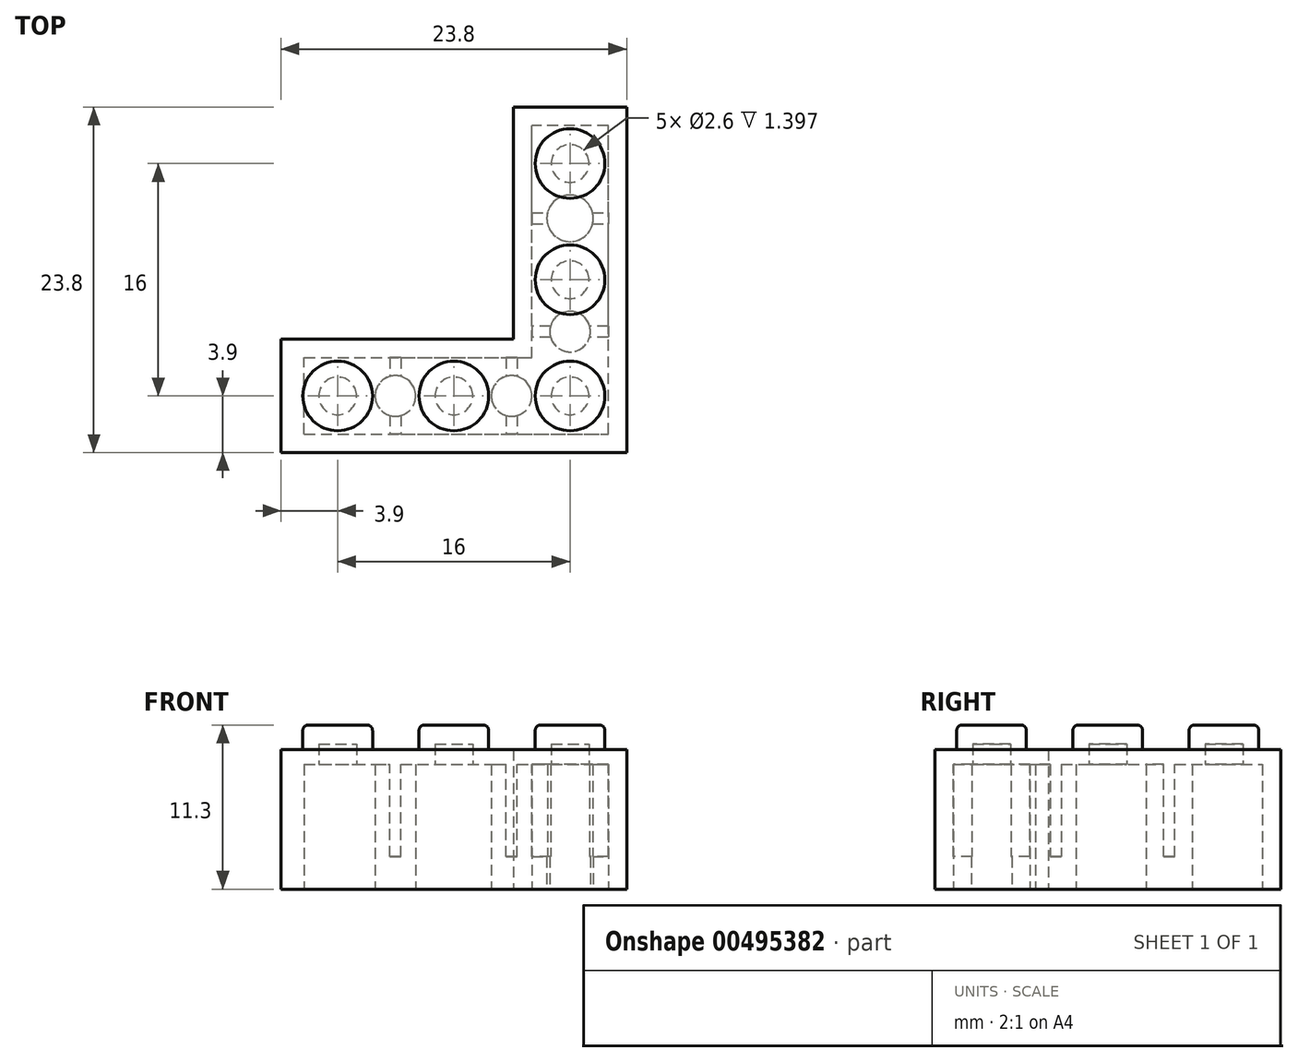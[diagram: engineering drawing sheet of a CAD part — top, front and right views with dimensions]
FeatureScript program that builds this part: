
annotation { "Feature Type Name" : "Feature", "Feature Type Description" : "" }
export const myFeature = defineFeature(function(context is Context, id is Id, definition is map)
    precondition{}
    {
        {
            var Q0;
            Q0=qCreatedBy(makeId("Top.planeOp"),FACE);
            var sketch = newSketch(context, id + "F0", { "sketchPlane" : qUnion([Q0])});
            skLineSegment(sketch, "E0.bottom", {"start": v(-16, 0) * mm, "end": v(0, 0) * mm});
            skLineSegment(sketch, "E0.top", {"start": v(-16, -7.8) * mm, "end": v(7.8, -7.8) * mm});
            skLineSegment(sketch, "E0.left", {"start": v(-16, 0) * mm, "end": v(-16, -7.8) * mm});
            skLineSegment(sketch, "E0.right", {"start": v(7.8, 0) * mm, "end": v(7.8, -7.8) * mm});
            skLineSegment(sketch, "E1.top", {"start": v(7.8, 16) * mm, "end": v(0, 16) * mm});
            skLineSegment(sketch, "E1.left", {"start": v(7.8, 0) * mm, "end": v(7.8, 16) * mm});
            skLineSegment(sketch, "E1.right", {"start": v(0, 0) * mm, "end": v(0, 16) * mm});
            skSolve(sketch);
        }
        {
            var Q0;
            Q0=makeQuery(id+"F0.imprint","IMPRINT",FACE,{"disambiguationData":[TD([[makeQuery(id+"F0.imprint","IMPRINT",EDGE,{"derivedFrom":sQuery(id+"F0.wireOp",EDGE,"E0.bottom")}),-1.0]])]});
            extrude(context, id + "F1", {"entities" : qUnion([Q0]), "depth" : 9.6 * mm});
        }
        {
            var Q0;
            Q0=makeQuery(id+"F1.opExtrude","CAP_FACE",FACE,{"disambiguationData":[OSD([sQuery(id+"F0.wireOp",EDGE,"E0.bottom"),sQuery(id+"F0.wireOp",EDGE,"E0.top"),sQuery(id+"F0.wireOp",EDGE,"E0.left"),sQuery(id+"F0.wireOp",EDGE,"E0.right"),sQuery(id+"F0.wireOp",EDGE,"E1.top"),sQuery(id+"F0.wireOp",EDGE,"E1.left"),sQuery(id+"F0.wireOp",EDGE,"E1.right")])],"isStart":false});
            var sketch = newSketch(context, id + "F2", { "sketchPlane" : qUnion([Q0])});
            skCircle(sketch, "E2", {"center": v(-12.1, -3.9) * mm, "radius": 2.4 * mm});
            skCircle(sketch, "E3", {"center": v(-4.1, -3.9) * mm, "radius": 2.4 * mm});
            skCircle(sketch, "E4", {"center": v(3.9, -3.9) * mm, "radius": 2.4 * mm});
            skCircle(sketch, "E5", {"center": v(3.9, 4.1) * mm, "radius": 2.4 * mm});
            skCircle(sketch, "E6", {"center": v(3.9, 12.1) * mm, "radius": 2.4 * mm});
            skLineSegment(sketch, "E7", {"start": v(-16, -3.9) * mm, "end": v(7.8, -3.9) * mm, "construction": true});
            skLineSegment(sketch, "E8", {"start": v(3.9, 16) * mm, "end": v(3.9, -7.8) * mm, "construction": true});
            skSolve(sketch);
        }
        {
            var Q0;
            Q0=qSketchRegion(id+"F2",true);
            extrude(context, id + "F3", {"entities" : qUnion([Q0]), "operationType" : NewBodyOperationType.ADD, "depth" : 1.7 * mm});
        }
        {
            var Q0;
            Q0=makeQuery(id+"F3.opExtrude","CAP_EDGE",EDGE,{"disambiguationData":[OSD([sQuery(id+"F2.wireOp",EDGE,"E6")])],"isStart":false});
            var Q1;
            Q1=makeQuery(id+"F3.opExtrude","CAP_EDGE",EDGE,{"disambiguationData":[OSD([sQuery(id+"F2.wireOp",EDGE,"E5")])],"isStart":false});
            var Q2;
            Q2=makeQuery(id+"F3.opExtrude","CAP_EDGE",EDGE,{"disambiguationData":[OSD([sQuery(id+"F2.wireOp",EDGE,"E4")])],"isStart":false});
            var Q3;
            Q3=makeQuery(id+"F3.opExtrude","CAP_EDGE",EDGE,{"disambiguationData":[OSD([sQuery(id+"F2.wireOp",EDGE,"E3")])],"isStart":false});
            var Q4;
            Q4=makeQuery(id+"F3.opExtrude","CAP_EDGE",EDGE,{"disambiguationData":[OSD([sQuery(id+"F2.wireOp",EDGE,"E2")])],"isStart":false});
            fillet(context, id + "F4", {"entities" : qUnion([Q0, Q1, Q2, Q3, Q4]), "radius" : 0.38 * mm, "tangentPropagation" : true, "allowEdgeOverflow" : false});
        }
        {
            var Q0;
            Q0=makeQuery(id+"F1.opExtrude","CAP_FACE",FACE,{"disambiguationData":[OSD([sQuery(id+"F0.wireOp",EDGE,"E0.bottom"),sQuery(id+"F0.wireOp",EDGE,"E0.top"),sQuery(id+"F0.wireOp",EDGE,"E0.left"),sQuery(id+"F0.wireOp",EDGE,"E0.right"),sQuery(id+"F0.wireOp",EDGE,"E1.top"),sQuery(id+"F0.wireOp",EDGE,"E1.left"),sQuery(id+"F0.wireOp",EDGE,"E1.right")])],"isStart":true});
            var sketch = newSketch(context, id + "F5", { "sketchPlane" : qUnion([Q0])});
            skLineSegment(sketch, "E9.bottom", {"start": v(-14.4, 6.53) * mm, "end": v(6.53, 6.53) * mm});
            skLineSegment(sketch, "E9.top", {"start": v(-14.4, 1.27) * mm, "end": v(1.27, 1.27) * mm});
            skLineSegment(sketch, "E9.left", {"start": v(-14.4, 6.53) * mm, "end": v(-14.4, 1.27) * mm});
            skLineSegment(sketch, "E9.right", {"start": v(6.53, 6.53) * mm, "end": v(6.53, 1.27) * mm});
            skLineSegment(sketch, "E10.top", {"start": v(6.53, -14.73) * mm, "end": v(1.27, -14.73) * mm});
            skLineSegment(sketch, "E10.left", {"start": v(6.53, 1.27) * mm, "end": v(6.53, -14.73) * mm});
            skLineSegment(sketch, "E10.right", {"start": v(1.27, 1.27) * mm, "end": v(1.27, -14.73) * mm});
            skCircle(sketch, "E11", {"center": v(-8.13, 3.9) * mm, "radius": 1.4 * mm});
            skCircle(sketch, "E12", {"center": v(-0.12, 3.9) * mm, "radius": 1.4 * mm});
            skCircle(sketch, "E13", {"center": v(3.9, -0.53) * mm, "radius": 1.4 * mm});
            skCircle(sketch, "E14", {"center": v(3.9, -8.33) * mm, "radius": 1.6 * mm});
            skLineSegment(sketch, "E15", {"start": v(-14.4, 3.9) * mm, "end": v(6.53, 3.9) * mm, "construction": true});
            skLineSegment(sketch, "E16", {"start": v(3.9, -14.73) * mm, "end": v(3.9, 6.53) * mm, "construction": true});
            skSolve(sketch);
        }
        {
            var Q0;
            Q0=makeQuery(id+"F5.imprint","IMPRINT",FACE,{"disambiguationData":[TD([[makeQuery(id+"F5.imprint","IMPRINT",EDGE,{"derivedFrom":sQuery(id+"F5.wireOp",EDGE,"E9.bottom")}),-1.0]])]});
            extrude(context, id + "F6", {"entities" : qUnion([Q0]), "operationType" : NewBodyOperationType.REMOVE, "oppositeDirection" : true, "depth" : 8.6 * mm});
        }
        {
            var Q0;
            Q0=makeQuery(id+"F6.boolean.opBoolean","COPY",FACE,{"derivedFrom":makeQuery(id+"F6.opExtrude","CAP_FACE",FACE,{"disambiguationData":[OSD([sQuery(id+"F5.wireOp",EDGE,"E9.bottom"),sQuery(id+"F5.wireOp",EDGE,"E9.top"),sQuery(id+"F5.wireOp",EDGE,"E9.left"),sQuery(id+"F5.wireOp",EDGE,"E9.right"),sQuery(id+"F5.wireOp",EDGE,"E10.top"),sQuery(id+"F5.wireOp",EDGE,"E10.left"),sQuery(id+"F5.wireOp",EDGE,"E10.right"),sQuery(id+"F5.wireOp",EDGE,"E11"),sQuery(id+"F5.wireOp",EDGE,"E12"),sQuery(id+"F5.wireOp",EDGE,"E13"),sQuery(id+"F5.wireOp",EDGE,"E14")])],"isStart":false})});
            var sketch = newSketch(context, id + "F7", { "sketchPlane" : qUnion([Q0])});
            skCircle(sketch, "E17", {"center": v(-12.1, 3.9) * mm, "radius": 1.3 * mm});
            skCircle(sketch, "E18", {"center": v(-4.1, 3.9) * mm, "radius": 1.3 * mm});
            skCircle(sketch, "E19", {"center": v(3.9, 3.9) * mm, "radius": 1.3 * mm});
            skCircle(sketch, "E20", {"center": v(3.9, -4.1) * mm, "radius": 1.3 * mm});
            skCircle(sketch, "E21", {"center": v(3.9, -12.1) * mm, "radius": 1.3 * mm});
            skSolve(sketch);
        }
        {
            var Q0;
            Q0=qSketchRegion(id+"F7",true);
            extrude(context, id + "F8", {"entities" : qUnion([Q0]), "operationType" : NewBodyOperationType.REMOVE, "oppositeDirection" : true, "depth" : 1.4 * mm});
        }
        {
            var Q0;
            Q0=makeQuery(id+"F6.boolean.opBoolean","COPY",FACE,{"derivedFrom":makeQuery(id+"F6.opExtrude","CAP_FACE",FACE,{"disambiguationData":[OSD([sQuery(id+"F5.wireOp",EDGE,"E9.bottom"),sQuery(id+"F5.wireOp",EDGE,"E9.top"),sQuery(id+"F5.wireOp",EDGE,"E9.left"),sQuery(id+"F5.wireOp",EDGE,"E9.right"),sQuery(id+"F5.wireOp",EDGE,"E10.top"),sQuery(id+"F5.wireOp",EDGE,"E10.left"),sQuery(id+"F5.wireOp",EDGE,"E10.right"),sQuery(id+"F5.wireOp",EDGE,"E11"),sQuery(id+"F5.wireOp",EDGE,"E12"),sQuery(id+"F5.wireOp",EDGE,"E13"),sQuery(id+"F5.wireOp",EDGE,"E14")])],"isStart":false})});
            var sketch = newSketch(context, id + "F9", { "sketchPlane" : qUnion([Q0])});
            skLineSegment(sketch, "E22", {"start": v(0.7, -8.33) * mm, "end": v(7.1, -8.33) * mm, "construction": true});
            skLineSegment(sketch, "E23", {"start": v(7.03, -0.53) * mm, "end": v(0.77, -0.53) * mm, "construction": true});
            skPoint(sketch, "E24", {"position": v(3.9, -0.53) * mm});
            skPoint(sketch, "E25", {"position": v(3.9, -8.33) * mm});
            skLineSegment(sketch, "E26.bottom", {"start": v(7.03, -0.15) * mm, "end": v(0.77, -0.15) * mm});
            skLineSegment(sketch, "E26.top", {"start": v(7.03, -0.91) * mm, "end": v(0.77, -0.91) * mm});
            skLineSegment(sketch, "E26.left", {"start": v(7.03, -0.15) * mm, "end": v(7.03, -0.91) * mm});
            skLineSegment(sketch, "E26.right", {"start": v(0.77, -0.15) * mm, "end": v(0.77, -0.91) * mm});
            skLineSegment(sketch, "E27.bottom", {"start": v(0.7, -7.95) * mm, "end": v(7.1, -7.95) * mm});
            skLineSegment(sketch, "E27.top", {"start": v(0.7, -8.7) * mm, "end": v(7.1, -8.7) * mm});
            skLineSegment(sketch, "E27.left", {"start": v(0.7, -7.95) * mm, "end": v(0.7, -8.7) * mm});
            skLineSegment(sketch, "E27.right", {"start": v(7.1, -7.95) * mm, "end": v(7.1, -8.7) * mm});
            skLineSegment(sketch, "E28.bottom", {"start": v(-7.74, 0.6) * mm, "end": v(-8.5, 0.6) * mm});
            skLineSegment(sketch, "E28.top", {"start": v(-7.74, 7.2) * mm, "end": v(-8.5, 7.2) * mm});
            skLineSegment(sketch, "E28.left", {"start": v(-7.74, 0.6) * mm, "end": v(-7.74, 7.2) * mm});
            skLineSegment(sketch, "E28.right", {"start": v(-8.5, 0.6) * mm, "end": v(-8.5, 7.2) * mm});
            skPoint(sketch, "E28.middle", {"position": v(-8.13, 3.9) * mm});
            skLineSegment(sketch, "E29.bottom", {"start": v(0.26, 0.71) * mm, "end": v(-0.5, 0.71) * mm});
            skLineSegment(sketch, "E29.top", {"start": v(0.26, 7.09) * mm, "end": v(-0.5, 7.09) * mm});
            skLineSegment(sketch, "E29.left", {"start": v(0.26, 0.71) * mm, "end": v(0.26, 7.09) * mm});
            skLineSegment(sketch, "E29.right", {"start": v(-0.5, 0.71) * mm, "end": v(-0.5, 7.09) * mm});
            skPoint(sketch, "E29.middle", {"position": v(-0.12, 3.9) * mm});
            skSolve(sketch);
        }
        {
            var Q0;
            Q0=qSketchRegion(id+"F9",true);
            extrude(context, id + "F10", {"entities" : qUnion([Q0]), "operationType" : NewBodyOperationType.ADD, "depth" : 6.35 * mm});
        }
    });
